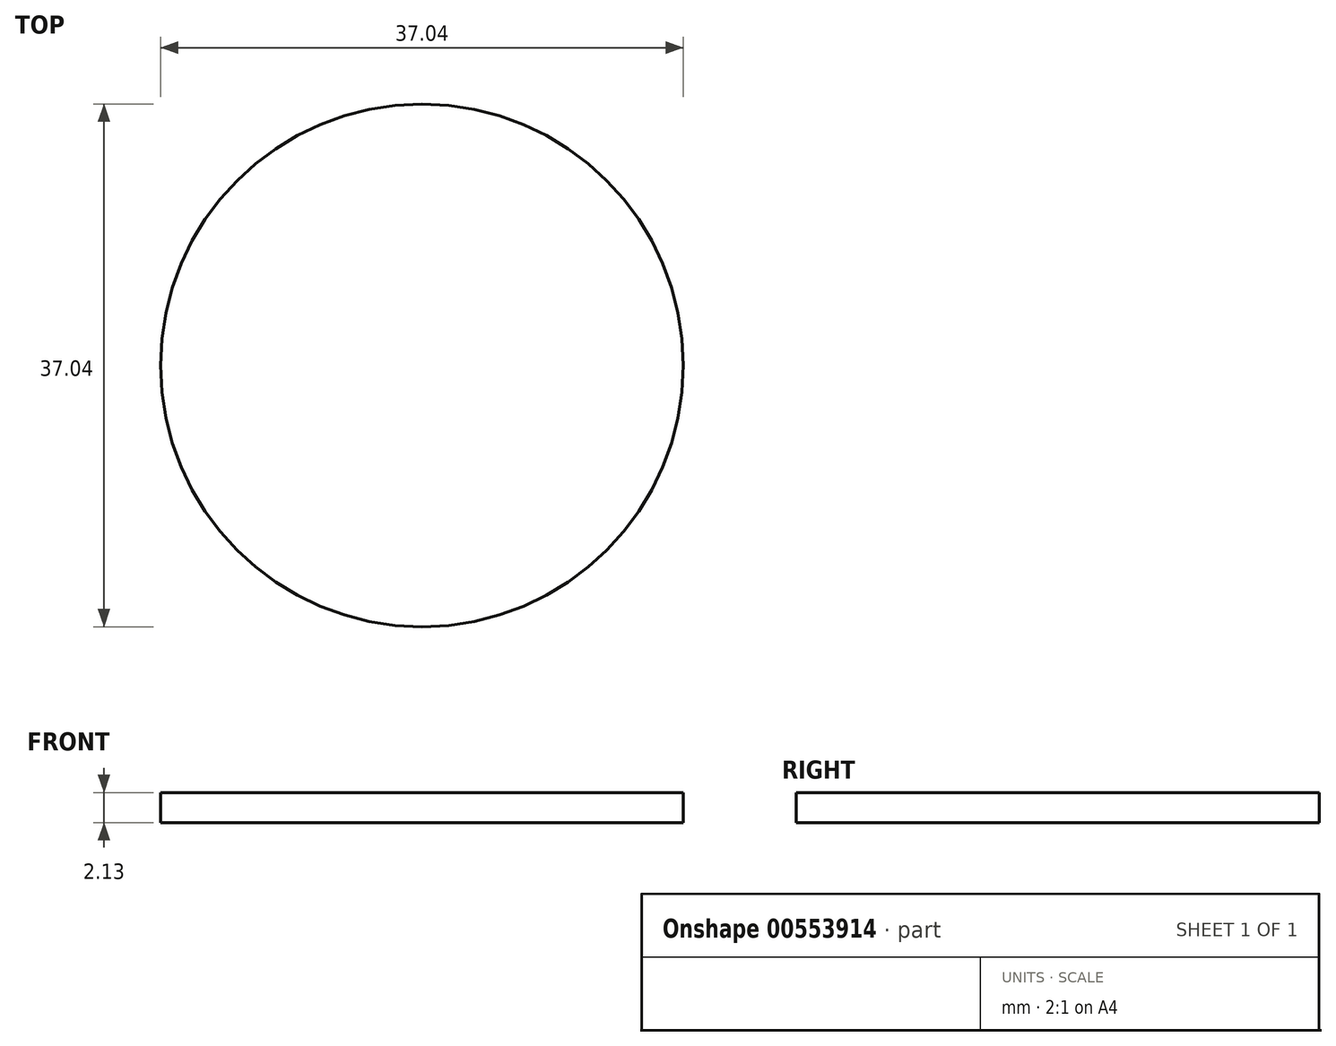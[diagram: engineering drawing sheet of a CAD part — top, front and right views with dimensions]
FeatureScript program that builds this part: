
annotation { "Feature Type Name" : "Feature", "Feature Type Description" : "" }
export const myFeature = defineFeature(function(context is Context, id is Id, definition is map)
    precondition{}
    {
        {
            var Q0;
            Q0=qCreatedBy(makeId("Front.planeOp"),FACE);
            var sketch = newSketch(context, id + "F0", { "sketchPlane" : qUnion([Q0])});
            skLineSegment(sketch, "E0.bottom", {"start": v(-18.52, 2.13) * mm, "end": v(21.48, 2.13) * mm});
            skLineSegment(sketch, "E0.top", {"start": v(-18.52, 0) * mm, "end": v(21.48, 0) * mm});
            skLineSegment(sketch, "E0.left", {"start": v(-18.52, 2.13) * mm, "end": v(-18.52, 0) * mm});
            skLineSegment(sketch, "E0.right", {"start": v(21.48, 2.13) * mm, "end": v(21.48, 0) * mm});
            skSolve(sketch);
        }
        {
            var Q0;
            Q0=makeQuery(id+"F0.imprint","IMPRINT",FACE,{"disambiguationData":[TD([[makeQuery(id+"F0.imprint","IMPRINT",EDGE,{"derivedFrom":sQuery(id+"F0.wireOp",EDGE,"E0.bottom")}),-1.0]])]});
            extrude(context, id + "F1", {"entities" : qUnion([Q0]), "endBound" : BoundingType.SYMMETRIC, "depth" : 40 * mm, "offsetDistance" : 25.4 * mm});
        }
        {
            var Q0;
            Q0=makeQuery(id+"F1.opExtrude","SWEPT_FACE",FACE,{"disambiguationData":[OSD([sQuery(id+"F0.wireOp",EDGE,"E0.bottom")])]});
            var sketch = newSketch(context, id + "F2", { "sketchPlane" : qUnion([Q0])});
            skCircle(sketch, "E1", {"center": v(0, 0) * mm, "radius": 18.52 * mm});
            skSolve(sketch);
        }
        {
            var Q0;
            Q0 = qSketchRegion(id + "F2", true);
            extrude(context, id + "F3", {"entities" : qUnion([Q0]), "operationType" : NewBodyOperationType.INTERSECT, "oppositeDirection" : true, "depth" : 25.4 * mm, "offsetDistance" : 25.4 * mm});
        }
    });
